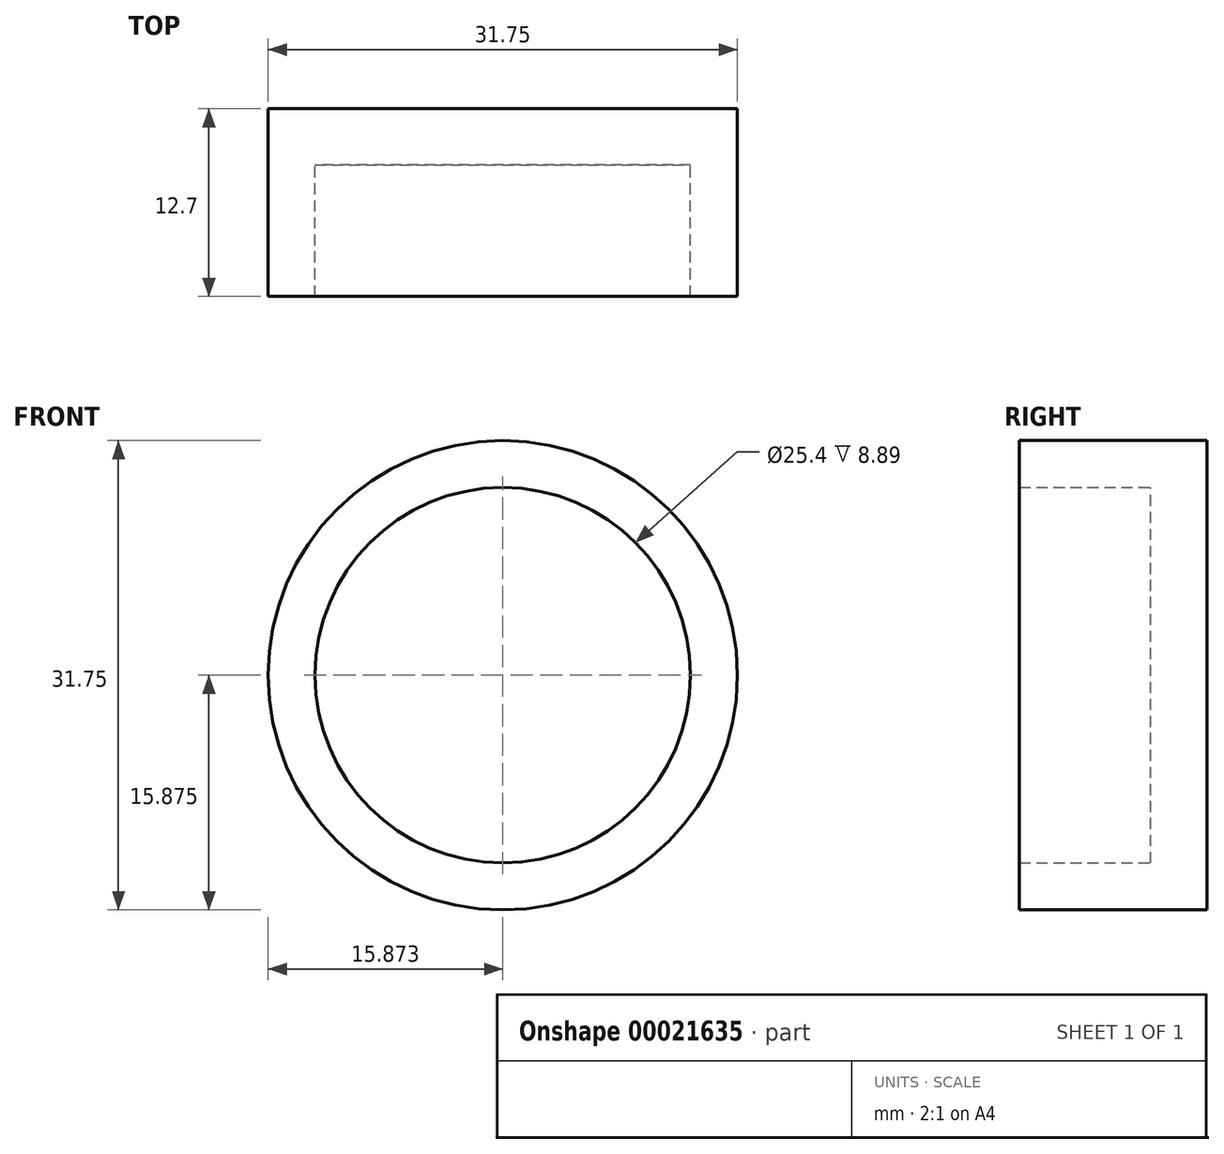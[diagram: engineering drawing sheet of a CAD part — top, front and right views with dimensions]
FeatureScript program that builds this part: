
annotation { "Feature Type Name" : "Feature", "Feature Type Description" : "" }
export const myFeature = defineFeature(function(context is Context, id is Id, definition is map)
    precondition{}
    {
        {
            var Q0;
            Q0=qCreatedBy(makeId("Front.planeOp"),FACE);
            var sketch = newSketch(context, id + "F0", { "sketchPlane" : qUnion([Q0])});
            skCircle(sketch, "E0", {"center": v(-606.42, 16.84) * mm, "radius": 12.7 * mm});
            skCircle(sketch, "E1", {"center": v(-606.42, 16.84) * mm, "radius": 15.88 * mm});
            skSolve(sketch);
        }
        {
            var Q0;
            Q0 = qSketchRegion(id + "F0", true);
            extrude(context, id + "F1", {"entities" : qUnion([Q0]), "depth" : 8.9 * mm});
        }
        {
            var Q0;
            Q0=makeQuery(id+"F0.imprint","IMPRINT",FACE,{"disambiguationData":[TD([[makeQuery(id+"F0.imprint","IMPRINT",EDGE,{"derivedFrom":sQuery(id+"F0.wireOp",EDGE,"E0")}),1.0]])]});
            var Q1;
            Q1=makeQuery(id+"F0.imprint","IMPRINT",FACE,{"disambiguationData":[TD([[makeQuery(id+"F0.imprint","IMPRINT",EDGE,{"derivedFrom":sQuery(id+"F0.wireOp",EDGE,"E0")}),-1.0]])]});
            extrude(context, id + "F2", {"entities" : qUnion([Q0, Q1]), "operationType" : NewBodyOperationType.ADD, "oppositeDirection" : true, "depth" : 3.8 * mm});
        }
    });
